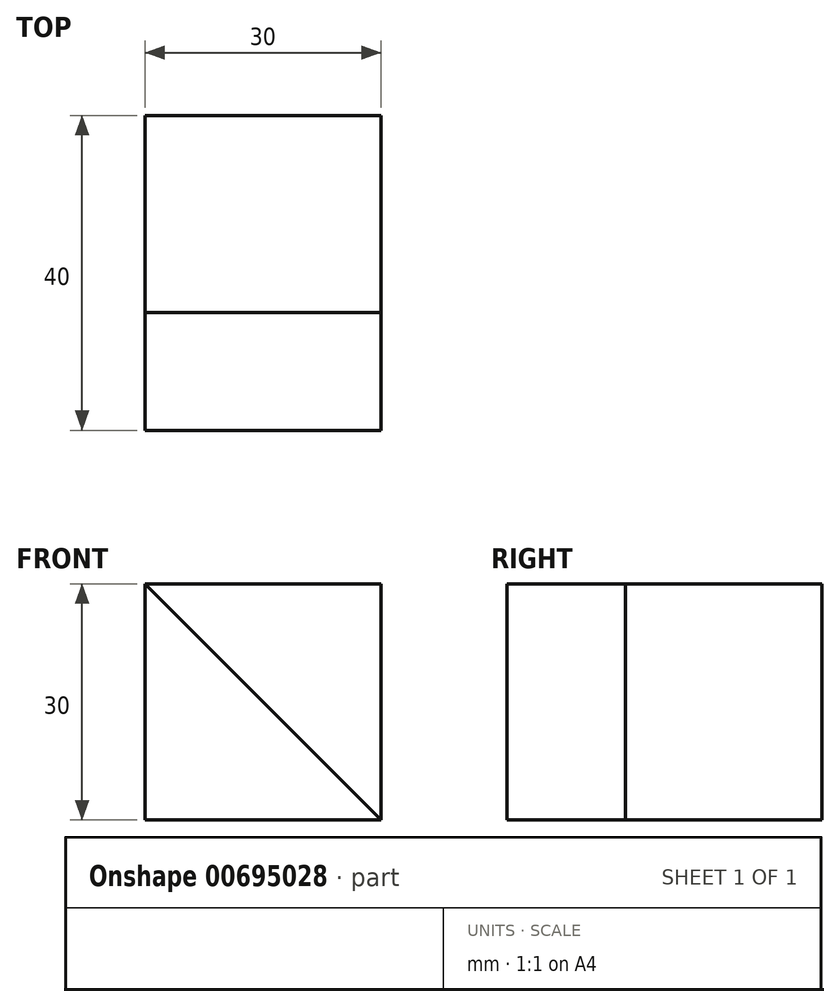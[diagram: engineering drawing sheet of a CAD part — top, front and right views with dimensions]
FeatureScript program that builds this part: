
annotation { "Feature Type Name" : "Feature", "Feature Type Description" : "" }
export const myFeature = defineFeature(function(context is Context, id is Id, definition is map)
    precondition{}
    {
        {
            var Q0;
            Q0=qCreatedBy(makeId("Front.planeOp"),FACE);
            var sketch = newSketch(context, id + "F0", { "sketchPlane" : qUnion([Q0])});
            skLineSegment(sketch, "E0", {"start": v(0, 0) * mm, "end": v(0, 30) * mm});
            skLineSegment(sketch, "E1", {"start": v(0, 0) * mm, "end": v(30, 0) * mm});
            skLineSegment(sketch, "E2", {"start": v(30, 0) * mm, "end": v(0, 30) * mm});
            skSolve(sketch);
        }
        {
            var Q0;
            Q0 = qSketchRegion(id + "F0", true);
            extrude(context, id + "F1", {"entities" : qUnion([Q0]), "oppositeDirection" : true, "depth" : 15 * mm, "offsetDistance" : 25 * mm});
        }
        {
            var Q0;
            Q0=qCreatedBy(makeId("Front.planeOp"),FACE);
            cPlane(context, id + "F2", {"entities" : qUnion([Q0]), "cplaneType" : CPlaneType.OFFSET, "offset" : 15 * mm, "oppositeDirection" : true, "width" : 150 * mm, "height" : 150 * mm});
        }
        {
            var Q0;
            Q0=qCreatedBy(id+"F2.planeOp",FACE);
            var sketch = newSketch(context, id + "F3", { "sketchPlane" : qUnion([Q0])});
            skLineSegment(sketch, "E3.bottom", {"start": v(0, 0) * mm, "end": v(30, 0) * mm});
            skLineSegment(sketch, "E3.top", {"start": v(0, 30) * mm, "end": v(30, 30) * mm});
            skLineSegment(sketch, "E3.left", {"start": v(0, 0) * mm, "end": v(0, 30) * mm});
            skLineSegment(sketch, "E3.right", {"start": v(30, 0) * mm, "end": v(30, 30) * mm});
            skSolve(sketch);
        }
        {
            var Q0;
            Q0=makeQuery(id+"F3.imprint","IMPRINT",FACE,{"disambiguationData":[TD([[makeQuery(id+"F3.imprint","IMPRINT",EDGE,{"derivedFrom":sQuery(id+"F3.wireOp",EDGE,"E3.bottom")}),1.0]])]});
            extrude(context, id + "F4", {"entities" : qUnion([Q0]), "operationType" : NewBodyOperationType.ADD, "oppositeDirection" : true, "depth" : 25 * mm, "offsetDistance" : 25 * mm});
        }
    });
